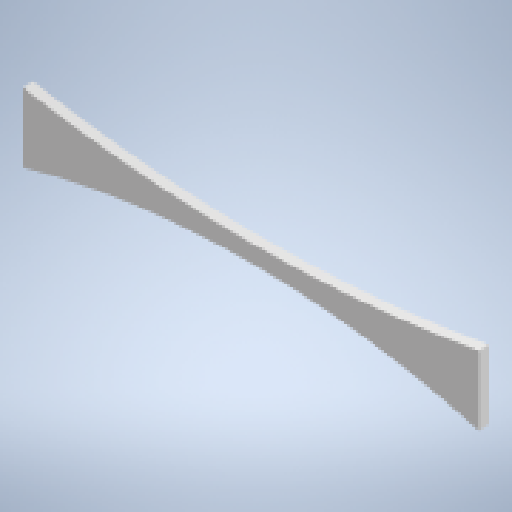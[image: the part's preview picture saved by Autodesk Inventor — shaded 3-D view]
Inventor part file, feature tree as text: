
AUTODESK INVENTOR PART (.ipt)
format: ipt  version: 2023 (Build 270158000, 158)  size: 145,408 bytes
history: native  units: mm
features: other x4, extrude x2, sketch x2, reference x2
ambient origin geometry x8: Origin, YZ Plane, XZ Plane, XY Plane, X Axis, Y Axis, Z Axis, Center Point
bodies: Solid1 (feature_tree)
feature tree (10):
  extrude  "Extrusion1"  Depth=132.15mm
  extrude  "Extrusion2"  Depth=3.0mm
  sketch  "Sketch1"  dims[d0=132.15mm d1=20.0mm]
  reference  "Reference1"
  reference  "Reference2"
  sketch  "Sketch2"  dims[d2=3.0mm d3=0.0mm d4=5.0mm d5=0.0mm d6=0.0mm]
  parser-record x1  (decoder bookkeeping rows leaked as tree rows — omitted from the tree; the rows remain in map.json)
  other  "Assembly.iam"
  other  "Album:1"
  other  "coverHolder:1"
note: 1 file-system path scrubbed to <path> (originals preserved in map.json)
